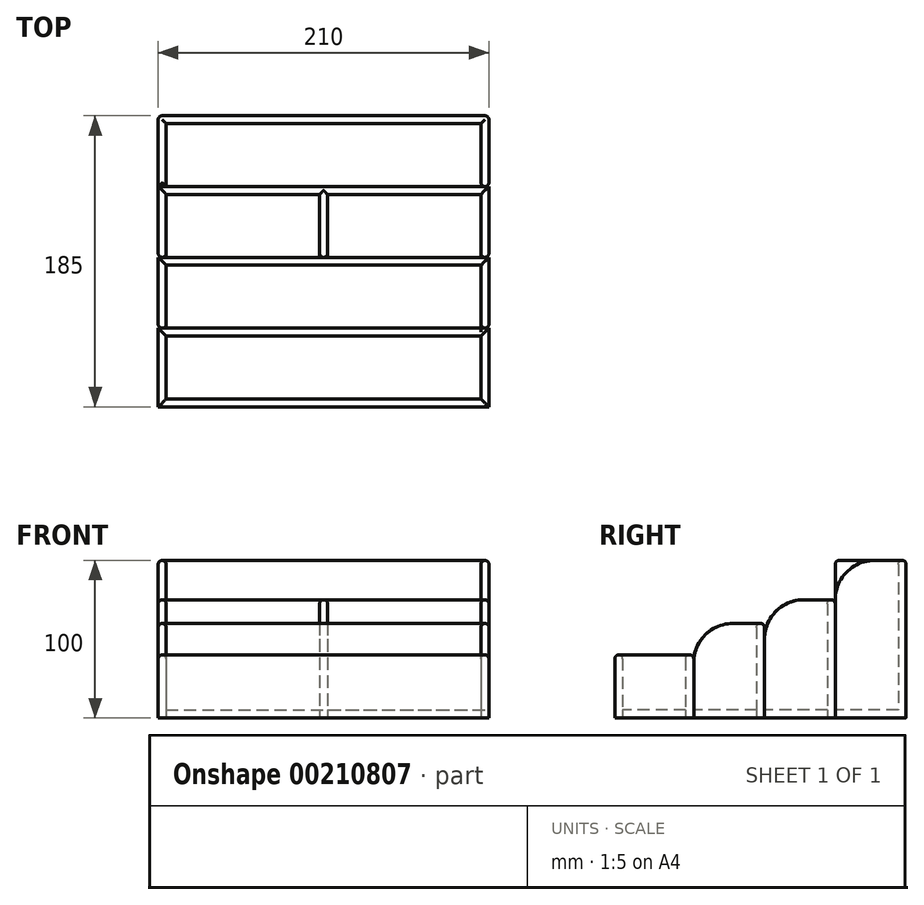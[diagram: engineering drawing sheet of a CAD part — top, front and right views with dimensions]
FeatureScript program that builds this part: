
annotation { "Feature Type Name" : "Feature", "Feature Type Description" : "" }
export const myFeature = defineFeature(function(context is Context, id is Id, definition is map)
    precondition{}
    {
        {
            var Q0;
            Q0=qCreatedBy(makeId("Top.planeOp"),FACE);
            var sketch = newSketch(context, id + "F0", { "sketchPlane" : qUnion([Q0])});
            skLineSegment(sketch, "E0.bottom", {"start": v(-97.5, 62.37) * mm, "end": v(102.5, 62.37) * mm});
            skLineSegment(sketch, "E0.top", {"start": v(-97.5, 22.37) * mm, "end": v(102.5, 22.37) * mm});
            skLineSegment(sketch, "E0.left", {"start": v(-97.5, 62.37) * mm, "end": v(-97.5, 22.37) * mm});
            skLineSegment(sketch, "E0.right", {"start": v(102.5, 62.37) * mm, "end": v(102.5, 22.37) * mm});
            skLineSegment(sketch, "E1.bottom", {"start": v(-97.5, 17.37) * mm, "end": v(0, 17.37) * mm});
            skLineSegment(sketch, "E1.top", {"start": v(-97.5, -22.63) * mm, "end": v(0, -22.63) * mm});
            skLineSegment(sketch, "E1.left", {"start": v(-97.5, 17.37) * mm, "end": v(-97.5, -22.63) * mm});
            skLineSegment(sketch, "E1.right", {"start": v(0, 17.37) * mm, "end": v(0, -22.63) * mm});
            skLineSegment(sketch, "E2.bottom", {"start": v(5, 17.37) * mm, "end": v(102.5, 17.37) * mm});
            skLineSegment(sketch, "E2.top", {"start": v(5, -22.63) * mm, "end": v(102.5, -22.63) * mm});
            skLineSegment(sketch, "E2.left", {"start": v(5, 17.37) * mm, "end": v(5, -22.63) * mm});
            skLineSegment(sketch, "E2.right", {"start": v(102.5, 17.37) * mm, "end": v(102.5, -22.63) * mm});
            skPoint(sketch, "E3.firstSnap0", {"position": v(-97.5, -2.63) * mm});
            skLineSegment(sketch, "E3.bottom", {"start": v(-97.5, -27.63) * mm, "end": v(102.5, -27.63) * mm});
            skLineSegment(sketch, "E3.top", {"start": v(-97.5, -67.63) * mm, "end": v(102.5, -67.63) * mm});
            skLineSegment(sketch, "E3.left", {"start": v(-97.5, -27.63) * mm, "end": v(-97.5, -67.63) * mm});
            skLineSegment(sketch, "E3.right", {"start": v(102.5, -27.63) * mm, "end": v(102.5, -67.63) * mm});
            skLineSegment(sketch, "E4.bottom", {"start": v(-97.5, -72.63) * mm, "end": v(102.5, -72.63) * mm});
            skLineSegment(sketch, "E4.top", {"start": v(-97.5, -112.63) * mm, "end": v(102.5, -112.63) * mm});
            skLineSegment(sketch, "E4.left", {"start": v(-97.5, -72.63) * mm, "end": v(-97.5, -112.63) * mm});
            skLineSegment(sketch, "E4.right", {"start": v(102.5, -72.63) * mm, "end": v(102.5, -112.63) * mm});
            skLineSegment(sketch, "E5.bottom", {"start": v(-102.5, 67.37) * mm, "end": v(107.5, 67.37) * mm});
            skLineSegment(sketch, "E5.top", {"start": v(-102.5, -117.63) * mm, "end": v(107.5, -117.63) * mm});
            skLineSegment(sketch, "E5.left", {"start": v(-102.5, 67.37) * mm, "end": v(-102.5, -117.63) * mm});
            skLineSegment(sketch, "E5.right", {"start": v(107.5, 67.37) * mm, "end": v(107.5, -117.63) * mm});
            skLineSegment(sketch, "E6", {"start": v(-97.5, 22.37) * mm, "end": v(-102.5, 22.37) * mm});
            skLineSegment(sketch, "E7", {"start": v(-102.5, 22.37) * mm, "end": v(102.5, 22.37) * mm});
            skLineSegment(sketch, "E8", {"start": v(-97.5, -22.63) * mm, "end": v(-102.5, -22.63) * mm});
            skLineSegment(sketch, "E9", {"start": v(-102.5, -22.63) * mm, "end": v(-102.5, 22.37) * mm});
            skLineSegment(sketch, "E10", {"start": v(-102.5, 17.5) * mm, "end": v(-97.5, 17.37) * mm});
            skLineSegment(sketch, "E11", {"start": v(102.5, 17.37) * mm, "end": v(107.5, 17.37) * mm});
            skLineSegment(sketch, "E12", {"start": v(107.5, 17.37) * mm, "end": v(107.5, -22.63) * mm});
            skLineSegment(sketch, "E13", {"start": v(107.5, -22.63) * mm, "end": v(102.5, -22.63) * mm});
            skLineSegment(sketch, "E14", {"start": v(102.5, -27.63) * mm, "end": v(107.5, -27.63) * mm});
            skLineSegment(sketch, "E15", {"start": v(107.5, -27.63) * mm, "end": v(107.5, -67.52) * mm});
            skLineSegment(sketch, "E16", {"start": v(107.5, -67.52) * mm, "end": v(102.5, -67.63) * mm});
            skLineSegment(sketch, "E17", {"start": v(102.5, -72.63) * mm, "end": v(107.5, -72.63) * mm});
            skLineSegment(sketch, "E18", {"start": v(107.5, -72.63) * mm, "end": v(-102.5, -72.63) * mm});
            skLineSegment(sketch, "E19", {"start": v(-102.5, -72.63) * mm, "end": v(-102.5, -67.63) * mm});
            skLineSegment(sketch, "E20", {"start": v(-102.5, -67.63) * mm, "end": v(-97.5, -67.63) * mm});
            skLineSegment(sketch, "E21", {"start": v(-97.5, -27.63) * mm, "end": v(-102.5, -27.63) * mm});
            skLineSegment(sketch, "E22", {"start": v(-102.5, -27.63) * mm, "end": v(-102.5, 22.37) * mm});
            skLineSegment(sketch, "E23", {"start": v(102.5, 22.37) * mm, "end": v(107.5, 22.37) * mm});
            skLineSegment(sketch, "E24", {"start": v(0, 17.37) * mm, "end": v(5, 17.37) * mm});
            skLineSegment(sketch, "E25", {"start": v(0, -22.63) * mm, "end": v(5, -22.63) * mm});
            skSolve(sketch);
        }
        {
            var Q0;
            Q0=makeQuery(id+"F0.imprint","IMPRINT",FACE,{"disambiguationData":[TD([[makeQuery(id+"F0.imprint","IMPRINT",EDGE,{"derivedFrom":sQuery(id+"F0.wireOp",EDGE,"E0.bottom")}),-1.0]])]});
            var Q1;
            Q1=makeQuery(id+"F0.imprint","IMPRINT",FACE,{"disambiguationData":[TD([[makeQuery(id+"F0.imprint","IMPRINT",EDGE,{"derivedFrom":sQuery(id+"F0.wireOp",EDGE,"E1.bottom")}),-1.0]])]});
            var Q2;
            Q2=makeQuery(id+"F0.imprint","IMPRINT",FACE,{"disambiguationData":[TD([[makeQuery(id+"F0.imprint","IMPRINT",EDGE,{"derivedFrom":sQuery(id+"F0.wireOp",EDGE,"E2.bottom")}),-1.0]])]});
            var Q3;
            Q3=makeQuery(id+"F0.imprint","IMPRINT",FACE,{"disambiguationData":[TD([[makeQuery(id+"F0.imprint","IMPRINT",EDGE,{"derivedFrom":sQuery(id+"F0.wireOp",EDGE,"E3.bottom")}),-1.0]])]});
            var Q4;
            Q4=makeQuery(id+"F0.imprint","IMPRINT",FACE,{"disambiguationData":[TD([[makeQuery(id+"F0.imprint","IMPRINT",EDGE,{"derivedFrom":sQuery(id+"F0.wireOp",EDGE,"E4.bottom")}),-1.0]])]});
            var Q5;
            Q5=makeQuery(id+"F0.imprint","IMPRINT",FACE,{"disambiguationData":[TD([[makeQuery(id+"F0.imprint","IMPRINT",EDGE,{"derivedFrom":sQuery(id+"F0.wireOp",EDGE,"E4.top")}),1.0]])]});
            extrude(context, id + "F1", {"entities" : qUnion([Q0, Q1, Q2, Q3, Q4, Q5]), "depth" : 5 * mm});
        }
        {
            var Q0;
            Q0=makeQuery(id+"F0.imprint","IMPRINT",FACE,{"disambiguationData":[TD([[makeQuery(id+"F0.imprint","IMPRINT",EDGE,{"derivedFrom":sQuery(id+"F0.wireOp",EDGE,"E0.bottom")}),1.0]])]});
            extrude(context, id + "F2", {"entities" : qUnion([Q0]), "operationType" : NewBodyOperationType.ADD, "depth" : 100 * mm});
        }
        {
            var Q0;
            Q0=makeQuery(id+"F0.imprint","IMPRINT",FACE,{"disambiguationData":[TD([[makeQuery(id+"F0.imprint","IMPRINT",EDGE,{"derivedFrom":sQuery(id+"F0.wireOp",EDGE,"E1.bottom")}),1.0]])]});
            var Q1;
            Q1=makeQuery(id+"F0.imprint","IMPRINT",FACE,{"disambiguationData":[TD([[makeQuery(id+"F0.imprint","IMPRINT",EDGE,{"derivedFrom":sQuery(id+"F0.wireOp",EDGE,"E2.right")}),1.0]])]});
            var Q2;
            Q2=makeQuery(id+"F0.imprint","IMPRINT",FACE,{"disambiguationData":[TD([[makeQuery(id+"F0.imprint","IMPRINT",EDGE,{"derivedFrom":sQuery(id+"F0.wireOp",EDGE,"E1.left")}),-1.0]])]});
            var Q3;
            Q3=makeQuery(id+"F0.imprint","IMPRINT",FACE,{"disambiguationData":[TD([[makeQuery(id+"F0.imprint","IMPRINT",EDGE,{"derivedFrom":sQuery(id+"F0.wireOp",EDGE,"E1.right")}),1.0]])]});
            extrude(context, id + "F3", {"entities" : qUnion([Q0, Q1, Q2, Q3]), "depth" : 75 * mm});
        }
        {
            var Q0;
            Q0=makeQuery(id+"F0.imprint","IMPRINT",FACE,{"disambiguationData":[TD([[makeQuery(id+"F0.imprint","IMPRINT",EDGE,{"derivedFrom":sQuery(id+"F0.wireOp",EDGE,"E1.top")}),-1.0]])]});
            var Q1;
            Q1=makeQuery(id+"F0.imprint","IMPRINT",FACE,{"disambiguationData":[TD([[makeQuery(id+"F0.imprint","IMPRINT",EDGE,{"derivedFrom":sQuery(id+"F0.wireOp",EDGE,"E3.left")}),-1.0]])]});
            var Q2;
            Q2=makeQuery(id+"F0.imprint","IMPRINT",FACE,{"disambiguationData":[TD([[makeQuery(id+"F0.imprint","IMPRINT",EDGE,{"derivedFrom":sQuery(id+"F0.wireOp",EDGE,"E3.right")}),1.0]])]});
            extrude(context, id + "F4", {"entities" : qUnion([Q0, Q1, Q2]), "depth" : 60 * mm});
        }
        {
            var Q0;
            Q0=makeQuery(id+"F0.imprint","IMPRINT",FACE,{"disambiguationData":[TD([[makeQuery(id+"F0.imprint","IMPRINT",EDGE,{"derivedFrom":sQuery(id+"F0.wireOp",EDGE,"E4.top")}),-1.0]])]});
            var Q1;
            Q1=makeQuery(id+"F0.imprint","IMPRINT",FACE,{"disambiguationData":[TD([[makeQuery(id+"F0.imprint","IMPRINT",EDGE,{"derivedFrom":sQuery(id+"F0.wireOp",EDGE,"E3.top")}),-1.0]])]});
            extrude(context, id + "F5", {"entities" : qUnion([Q0, Q1]), "depth" : 40 * mm});
        }
        {
            var Q0;
            Q0=makeQuery(id+"F2.opExtrude","CAP_EDGE",EDGE,{"disambiguationData":[OSD([sQuery(id+"F0.wireOp",EDGE,"E7")])],"isStart":false});
            var Q1;
            Q1=makeQuery(id+"F2.opExtrude","CAP_EDGE",EDGE,{"disambiguationData":[OSD([sQuery(id+"F0.wireOp",EDGE,"E23")])],"isStart":false});
            var Q2;
            Q2=makeQuery(id+"F3.opExtrude","CAP_EDGE",EDGE,{"disambiguationData":[OSD([sQuery(id+"F0.wireOp",EDGE,"E13")])],"isStart":false});
            var Q3;
            Q3=makeQuery(id+"F4.opExtrude","CAP_EDGE",EDGE,{"disambiguationData":[OSD([sQuery(id+"F0.wireOp",EDGE,"E16")])],"isStart":false});
            var Q4;
            Q4=makeQuery(id+"F4.opExtrude","CAP_EDGE",EDGE,{"disambiguationData":[OSD([sQuery(id+"F0.wireOp",EDGE,"E20")])],"isStart":false});
            var Q5;
            Q5=makeQuery(id+"F3.opExtrude","CAP_EDGE",EDGE,{"disambiguationData":[OSD([sQuery(id+"F0.wireOp",EDGE,"E8")])],"isStart":false});
            var Q6;
            Q6=makeQuery(id+"F3.opExtrude","CAP_EDGE",EDGE,{"disambiguationData":[OSD([sQuery(id+"F0.wireOp",EDGE,"E25")])],"isStart":false});
            fillet(context, id + "F6", {"entities" : qUnion([Q0, Q1, Q2, Q3, Q4, Q5, Q6]), "radius" : 25 * mm, "tangentPropagation" : true, "allowEdgeOverflow" : false});
        }
        {
            var Q0;
            Q0=makeQuery(id+"F5.opExtrude","CAP_FACE",FACE,{"disambiguationData":[OSD([sQuery(id+"F0.wireOp",EDGE,"E3.top"),sQuery(id+"F0.wireOp",EDGE,"E4.top"),sQuery(id+"F0.wireOp",EDGE,"E4.left"),sQuery(id+"F0.wireOp",EDGE,"E4.right"),sQuery(id+"F0.wireOp",EDGE,"E5.top"),sQuery(id+"F0.wireOp",EDGE,"E5.left"),sQuery(id+"F0.wireOp",EDGE,"E5.right"),sQuery(id+"F0.wireOp",EDGE,"E16"),sQuery(id+"F0.wireOp",EDGE,"E18"),sQuery(id+"F0.wireOp",EDGE,"E19"),sQuery(id+"F0.wireOp",EDGE,"E20")])],"isStart":false});
            var Q1;
            Q1=makeQuery(id+"F6.opFillet","BLEND_FACE",FACE,{"disambiguationData":[OSD([sQuery(id+"F0.wireOp",EDGE,"E16")])]});
            var Q2;
            Q2=makeQuery(id+"F4.opExtrude","CAP_EDGE",EDGE,{"disambiguationData":[OSD([sQuery(id+"F0.wireOp",EDGE,"E3.bottom")])],"isStart":false});
            var Q3;
            Q3=makeQuery(id+"F4.opExtrude","CAP_FACE",FACE,{"disambiguationData":[OSD([sQuery(id+"F0.wireOp",EDGE,"E1.top"),sQuery(id+"F0.wireOp",EDGE,"E2.top"),sQuery(id+"F0.wireOp",EDGE,"E3.bottom"),sQuery(id+"F0.wireOp",EDGE,"E3.left"),sQuery(id+"F0.wireOp",EDGE,"E3.right"),sQuery(id+"F0.wireOp",EDGE,"E5.left"),sQuery(id+"F0.wireOp",EDGE,"E5.right"),sQuery(id+"F0.wireOp",EDGE,"E8"),sQuery(id+"F0.wireOp",EDGE,"E13"),sQuery(id+"F0.wireOp",EDGE,"E15"),sQuery(id+"F0.wireOp",EDGE,"E16"),sQuery(id+"F0.wireOp",EDGE,"E20"),sQuery(id+"F0.wireOp",EDGE,"E22"),sQuery(id+"F0.wireOp",EDGE,"E25")])],"isStart":false});
            var Q4;
            Q4=makeQuery(id+"F3.opExtrude","CAP_FACE",FACE,{"disambiguationData":[OSD([sQuery(id+"F0.wireOp",EDGE,"E1.bottom"),sQuery(id+"F0.wireOp",EDGE,"E1.left"),sQuery(id+"F0.wireOp",EDGE,"E1.right"),sQuery(id+"F0.wireOp",EDGE,"E2.bottom"),sQuery(id+"F0.wireOp",EDGE,"E2.left"),sQuery(id+"F0.wireOp",EDGE,"E2.right"),sQuery(id+"F0.wireOp",EDGE,"E5.right"),sQuery(id+"F0.wireOp",EDGE,"E7"),sQuery(id+"F0.wireOp",EDGE,"E8"),sQuery(id+"F0.wireOp",EDGE,"E12"),sQuery(id+"F0.wireOp",EDGE,"E13"),sQuery(id+"F0.wireOp",EDGE,"E22"),sQuery(id+"F0.wireOp",EDGE,"E23"),sQuery(id+"F0.wireOp",EDGE,"E25")])],"isStart":false});
            var Q5;
            Q5=makeQuery(id+"F2.opExtrude","CAP_FACE",FACE,{"disambiguationData":[OSD([sQuery(id+"F0.wireOp",EDGE,"E0.bottom"),sQuery(id+"F0.wireOp",EDGE,"E0.left"),sQuery(id+"F0.wireOp",EDGE,"E0.right"),sQuery(id+"F0.wireOp",EDGE,"E5.bottom"),sQuery(id+"F0.wireOp",EDGE,"E5.left"),sQuery(id+"F0.wireOp",EDGE,"E5.right"),sQuery(id+"F0.wireOp",EDGE,"E7"),sQuery(id+"F0.wireOp",EDGE,"E23")])],"isStart":false});
            var Q6;
            Q6=makeQuery(id+"F2.opExtrude","SWEPT_EDGE",EDGE,{"disambiguationData":[OSD([sQuery(id+"F0.wireOp",EDGE,"E5.bottom"),sQuery(id+"F0.wireOp",EDGE,"E5.right")])]});
            var Q7;
            Q7=makeQuery(id+"F2.opExtrude","SWEPT_EDGE",EDGE,{"disambiguationData":[OSD([sQuery(id+"F0.wireOp",EDGE,"E5.bottom"),sQuery(id+"F0.wireOp",EDGE,"E5.left")])]});
            fillet(context, id + "F7", {"entities" : qUnion([Q0, Q1, Q2, Q3, Q4, Q5, Q6, Q7]), "radius" : 2.5 * mm, "tangentPropagation" : true, "allowEdgeOverflow" : false});
        }
    });
